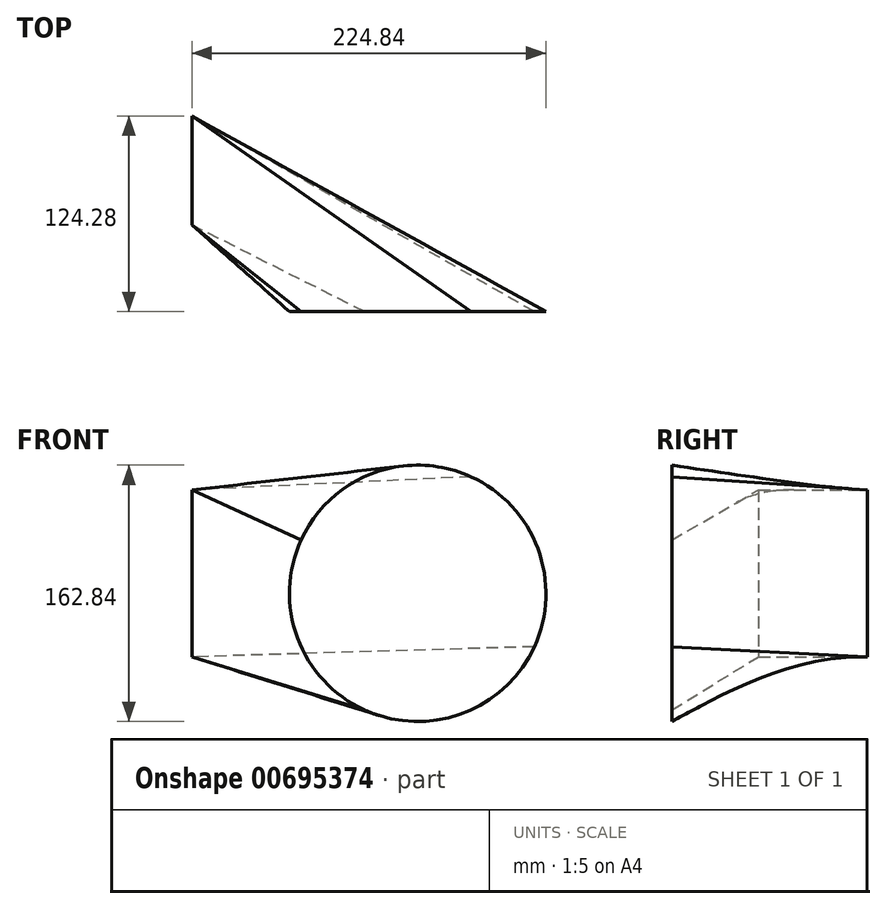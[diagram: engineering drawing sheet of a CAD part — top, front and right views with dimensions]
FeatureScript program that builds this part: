
annotation { "Feature Type Name" : "Feature", "Feature Type Description" : "" }
export const myFeature = defineFeature(function(context is Context, id is Id, definition is map)
    precondition{}
    {
        {
            var Q0;
            Q0=qCreatedBy(makeId("Front.planeOp"),FACE);
            var sketch = newSketch(context, id + "F0", { "sketchPlane" : qUnion([Q0])});
            skCircle(sketch, "E0", {"center": v(143.42, 0) * mm, "radius": 81.42 * mm});
            skSolve(sketch);
        }
        {
            var Q0;
            Q0=qCreatedBy(makeId("Right.planeOp"),FACE);
            var sketch = newSketch(context, id + "F1", { "sketchPlane" : qUnion([Q0])});
            skLineSegment(sketch, "E1.bottom", {"start": v(55.06, 65.68) * mm, "end": v(124.28, 65.68) * mm});
            skLineSegment(sketch, "E1.top", {"start": v(55.06, -40.37) * mm, "end": v(124.28, -40.37) * mm});
            skLineSegment(sketch, "E1.left", {"start": v(55.06, 65.68) * mm, "end": v(55.06, -40.37) * mm});
            skLineSegment(sketch, "E1.right", {"start": v(124.28, 65.68) * mm, "end": v(124.28, -40.37) * mm});
            skSolve(sketch);
        }
        {
            var Q0;
            Q0=makeQuery(id+"F0.imprint","IMPRINT",FACE,{"disambiguationData":[TD([[makeQuery(id+"F0.imprint","IMPRINT",EDGE,{"derivedFrom":sQuery(id+"F0.wireOp",EDGE,"E0")}),1.0]])]});
            var Q1;
            Q1=makeQuery(id+"F1.imprint","IMPRINT",FACE,{"disambiguationData":[TD([[makeQuery(id+"F1.imprint","IMPRINT",EDGE,{"derivedFrom":sQuery(id+"F1.wireOp",EDGE,"E1.bottom")}),-1.0]])]});
            loft(context, id + "F2", {"sheetProfilesArray" : [{ "sheetProfileEntities" : qUnion([Q0]) }, { "sheetProfileEntities" : qUnion([Q1]) }]});
        }
    });
